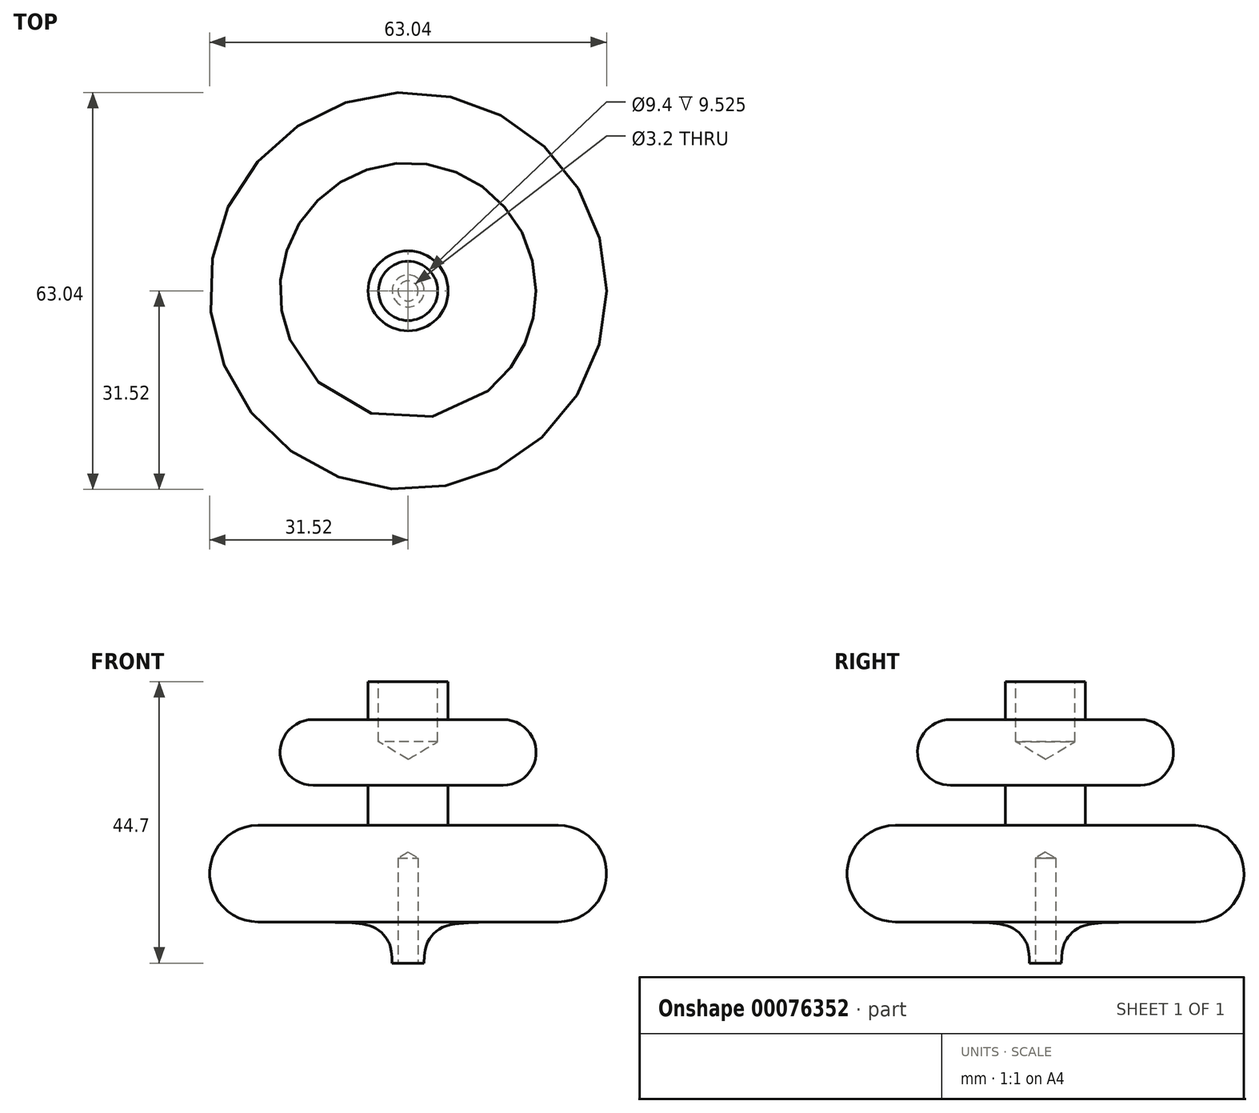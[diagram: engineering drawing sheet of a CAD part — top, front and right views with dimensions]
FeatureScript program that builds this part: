
annotation { "Feature Type Name" : "Feature", "Feature Type Description" : "" }
export const myFeature = defineFeature(function(context is Context, id is Id, definition is map)
    precondition{}
    {
        {
            var Q0;
            Q0=qCreatedBy(makeId("Front.planeOp"),FACE);
            var sketch = newSketch(context, id + "F0", { "sketchPlane" : qUnion([Q0])});
            skLineSegment(sketch, "E0", {"start": v(0, -21.87) * mm, "end": v(2.54, -21.87) * mm});
            skLineSegment(sketch, "E1", {"start": v(6.35, 0) * mm, "end": v(6.35, 6.35) * mm});
            skLineSegment(sketch, "E2", {"start": v(0, 22.83) * mm, "end": v(0, -21.87) * mm});
            skLineSegment(sketch, "E3", {"start": v(16.22, -15.33) * mm, "end": v(23.85, -15.33) * mm});
            skArc(sketch, "E4", {"start": v(23.85, -15.33) * mm, "mid": v(31.52, -7.66) * mm, "end": v(23.85, 0) * mm});
            skPoint(sketch, "E5.endSnap0", {"position": v(31.52, -7.66) * mm});
            skFitSpline(sketch, "E6", {"points": [v(2.54, -21.87) * mm, v(3.65, -17.66) * mm, v(5.55, -16.15) * mm, v(9.24, -15.49) * mm, v(16.22, -15.33) * mm], "startDerivative": vector(0.05, 29.66) * mm, "endDerivative": vector(29.16, 0.22) * mm});
            skLineSegment(sketch, "E7", {"start": v(6.35, 0) * mm, "end": v(23.85, 0) * mm});
            skLineSegment(sketch, "E8", {"start": v(6.35, 6.35) * mm, "end": v(15.1, 6.35) * mm});
            skArc(sketch, "E9", {"start": v(15.1, 6.35) * mm, "mid": v(20.33, 11.57) * mm, "end": v(15.1, 16.8) * mm});
            skLineSegment(sketch, "E10", {"start": v(6.35, 22.83) * mm, "end": v(0, 22.83) * mm});
            skLineSegment(sketch, "E11", {"start": v(6.35, 22.83) * mm, "end": v(6.35, 16.8) * mm});
            skLineSegment(sketch, "E12", {"start": v(6.35, 16.8) * mm, "end": v(15.1, 16.8) * mm});
            skSolve(sketch);
        }
        {
            var Q0;
            Q0=makeQuery(id+"F0.imprint","IMPRINT",FACE,{"disambiguationData":[TD([[makeQuery(id+"F0.imprint","IMPRINT",EDGE,{"derivedFrom":sQuery(id+"F0.wireOp",EDGE,"E0")}),1.0]])]});
            var Q1;
            Q1=sQuery(id+"F0.wireOp",EDGE,"E2");
            revolve(context, id + "F1", {"entities" : qUnion([Q0]), "axis" : qUnion([Q1]), "revolveType" : RevolveType.FULL});
        }
        {
            var Q0;
            Q0=makeQuery(id+"F1.opRevolve","SWEPT_FACE",FACE,{"disambiguationData":[OSD([sQuery(id+"F0.wireOp",EDGE,"E10")])]});
            var sketch = newSketch(context, id + "F2", { "sketchPlane" : qUnion([Q0])});
            skCircle(sketch, "E13", {"center": v(0, 0) * mm, "radius": 4.76 * mm});
            skSolve(sketch);
        }
        {
            var Q0;
            Q0=sQuery(id+"F2.wireOp",VERTEX,"E13.center");
            var Q1;
            Q1=makeQuery(id+"F1.opRevolve","SWEPT_BODY",BODY,{"disambiguationData":[OSD([sQuery(id+"F0.wireOp",EDGE,"E0"),sQuery(id+"F0.wireOp",EDGE,"E1"),sQuery(id+"F0.wireOp",EDGE,"74BJN9Fq-oJSt-7vEp-BQbR-2yZAhzl31MtC"),sQuery(id+"F0.wireOp",EDGE,"E2"),sQuery(id+"F0.wireOp",EDGE,"E3"),sQuery(id+"F0.wireOp",EDGE,"E4"),sQuery(id+"F0.wireOp",EDGE,"E6"),sQuery(id+"F0.wireOp",EDGE,"E7")])]});
            hole(context, id + "F3", {"style" : HoleStyle.SIMPLE, "endStyle" : HoleEndStyle.BLIND, "holeDiameter" : 9.4 * mm, "holeDepth" : 9.52 * mm, "startFromSketch" : true, "locations" : qUnion([Q0]), "scope" : qUnion([Q1])});
        }
        {
            var Q0;
            Q0=makeQuery(id+"F1.opRevolve","SWEPT_FACE",FACE,{"disambiguationData":[OSD([sQuery(id+"F0.wireOp",EDGE,"E0")])]});
            var sketch = newSketch(context, id + "F4", { "sketchPlane" : qUnion([Q0])});
            skCircle(sketch, "E14", {"center": v(0, 0) * mm, "radius": 1.6 * mm});
            skSolve(sketch);
        }
        {
            var Q0;
            Q0=sQuery(id+"F4.wireOp",VERTEX,"E14.center");
            var Q1;
            Q1=makeQuery(id+"F1.opRevolve","SWEPT_BODY",BODY,{"disambiguationData":[OSD([sQuery(id+"F0.wireOp",EDGE,"E0"),sQuery(id+"F0.wireOp",EDGE,"E1"),sQuery(id+"F0.wireOp",EDGE,"74BJN9Fq-oJSt-7vEp-BQbR-2yZAhzl31MtC"),sQuery(id+"F0.wireOp",EDGE,"E2"),sQuery(id+"F0.wireOp",EDGE,"E3"),sQuery(id+"F0.wireOp",EDGE,"E4"),sQuery(id+"F0.wireOp",EDGE,"E6"),sQuery(id+"F0.wireOp",EDGE,"E7")])]});
            hole(context, id + "F5", {"style" : HoleStyle.SIMPLE, "endStyle" : HoleEndStyle.BLIND, "holeDiameter" : 3.2 * mm, "holeDepth" : 16.67 * mm, "locations" : qUnion([Q0]), "scope" : qUnion([Q1])});
        }
    });
